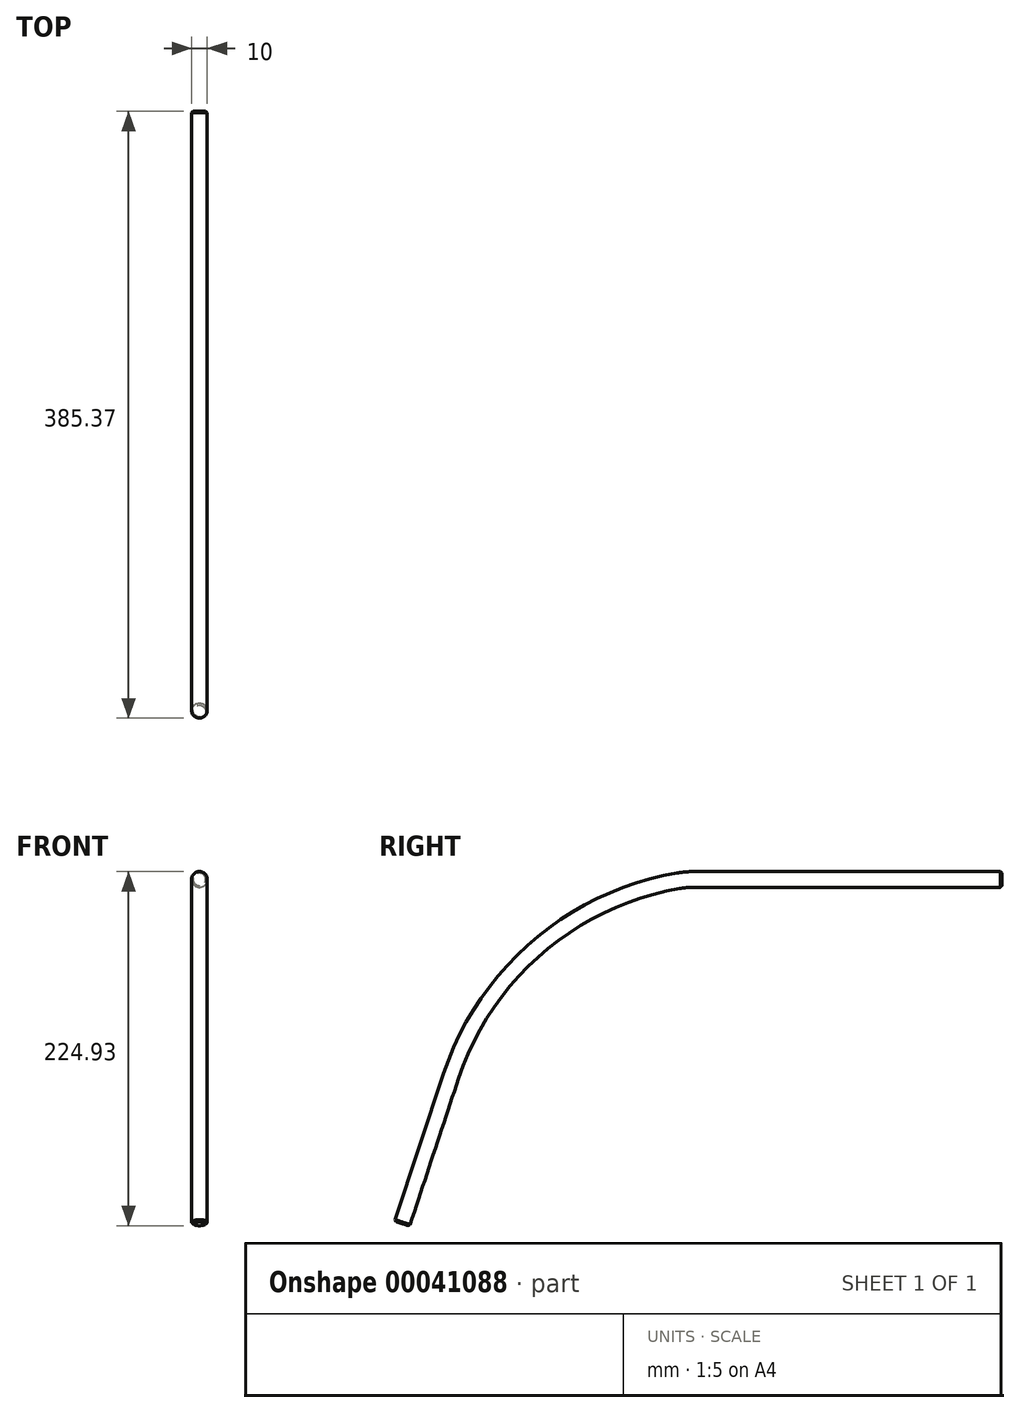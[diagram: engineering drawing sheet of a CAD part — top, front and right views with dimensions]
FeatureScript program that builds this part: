
annotation { "Feature Type Name" : "Feature", "Feature Type Description" : "" }
export const myFeature = defineFeature(function(context is Context, id is Id, definition is map)
    precondition{}
    {
        {
            var Q0;
            Q0=qCreatedBy(makeId("Right.planeOp"),FACE);
            var sketch = newSketch(context, id + "F0", { "sketchPlane" : qUnion([Q0])});
            skLineSegment(sketch, "E0", {"start": v(184.97, 68.13) * mm, "end": v(-10.44, 68.13) * mm});
            skArc(sketch, "E1", {"start": v(-20.54, 67.28) * mm, "mid": v(-109.99, 25.23) * mm, "end": v(-165.03, -56.87) * mm});
            skPoint(sketch, "E2.visualSharp", {"position": v(-15.03, 68.13) * mm});
            skArc(sketch, "E2.filletArc", {"start": v(-10.44, 68.13) * mm, "mid": v(-15.5, 67.92) * mm, "end": v(-20.54, 67.28) * mm});
            skPoint(sketch, "E3", {"position": v(184.97, 68.13) * mm});
            skPoint(sketch, "E4", {"position": v(-165.03, -56.87) * mm});
            skLineSegment(sketch, "E5", {"start": v(-165.03, -56.87) * mm, "end": v(-196.14, -150.65) * mm});
            skSolve(sketch);
        }
        {
            var Q0;
            Q0=qCreatedBy(makeId("Front.planeOp"),FACE);
            var Q1;
            Q1=sQuery(id+"F0.wireOp",VERTEX,"E3");
            cPlane(context, id + "F1", {"entities" : qUnion([Q0, Q1]), "cplaneType" : CPlaneType.PLANE_POINT, "offset" : 150 * mm, "width" : 150 * mm, "height" : 150 * mm});
        }
        {
            var Q0;
            Q0=qCreatedBy(id+"F1.planeOp",FACE);
            var sketch = newSketch(context, id + "F2", { "sketchPlane" : qUnion([Q0])});
            skCircle(sketch, "E6", {"center": v(0, 309.43) * mm, "radius": 5 * mm});
            skPoint(sketch, "E7", {"position": v(0, 67.96) * mm});
            skCircle(sketch, "E8", {"center": v(0, 67.96) * mm, "radius": 5 * mm});
            skSolve(sketch);
        }
        {
            var Q0;
            Q0=makeQuery(id+"F2.imprint","IMPRINT",FACE,{"disambiguationData":[TD([[makeQuery(id+"F2.imprint","IMPRINT",EDGE,{"derivedFrom":sQuery(id+"F2.wireOp",EDGE,"E8")}),1.0]])]});
            var Q1;
            Q1=sQuery(id+"F0.wireOp",EDGE,"E0");
            var Q2;
            Q2=sQuery(id+"F0.wireOp",EDGE,"E2.filletArc");
            var Q3;
            Q3=sQuery(id+"F0.wireOp",EDGE,"E1");
            var Q4;
            Q4=sQuery(id+"F0.wireOp",EDGE,"E5");
            sweep(context, id + "F3", {"profiles" : qUnion([Q0]), "path" : qUnion([Q1, Q2, Q3, Q4])});
        }
        {
            var Q0;
            Q0=makeQuery(id+"F3.opSweep","CAP_EDGE",EDGE,{"disambiguationData":[OSD([sQuery(id+"F0.wireOp",VERTEX,"E0.start"),sQuery(id+"F2.wireOp",EDGE,"E8")])],"isStart":true});
            var Q1;
            Q1=makeQuery(id+"F3.opSweep","CAP_EDGE",EDGE,{"disambiguationData":[OSD([sQuery(id+"F0.wireOp",VERTEX,"E5.end"),sQuery(id+"F2.wireOp",EDGE,"E8")])],"isStart":false});
            chamfer(context, id + "F4", {"entities" : qUnion([Q0, Q1]), "width" : 1 * mm, "tangentPropagation" : true});
        }
    });
